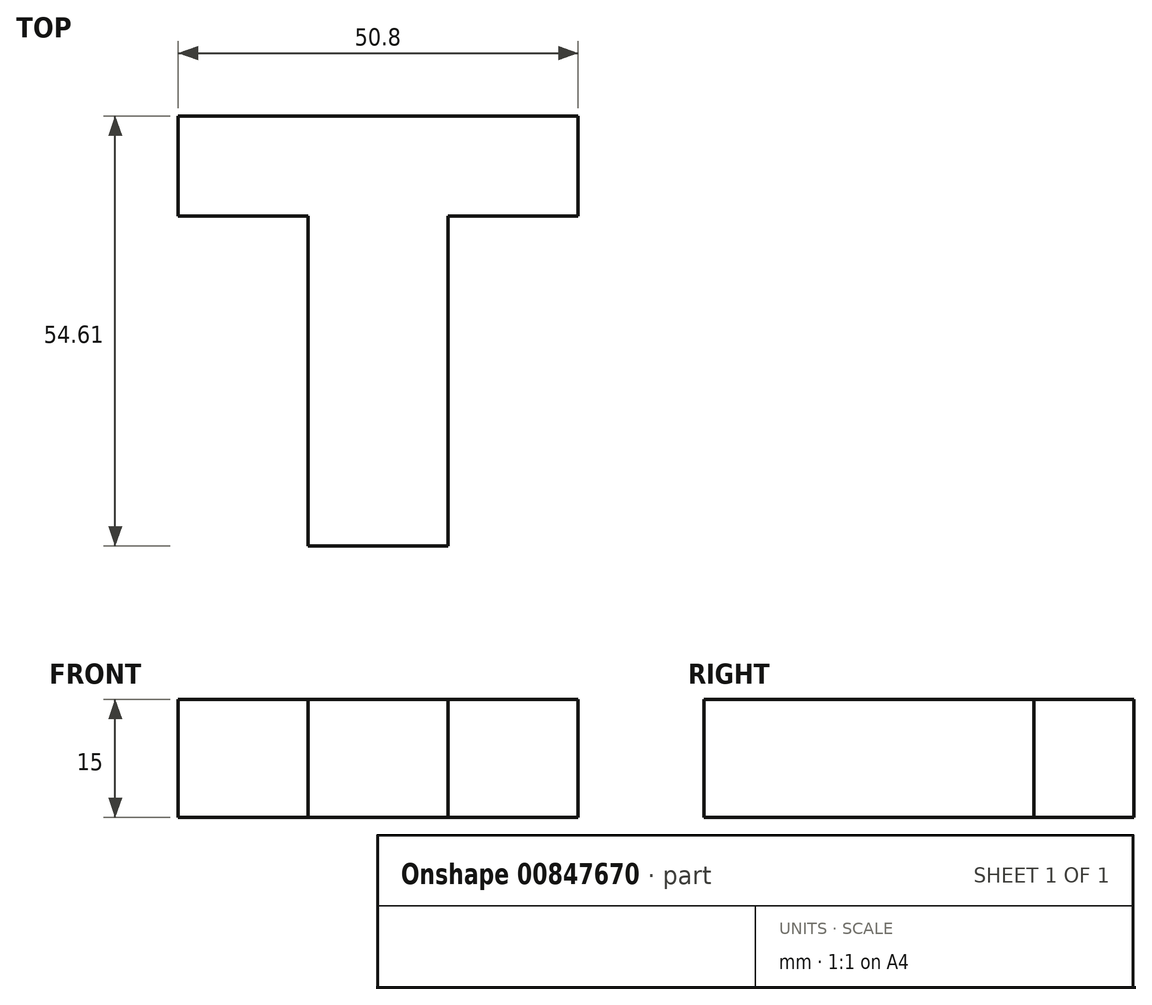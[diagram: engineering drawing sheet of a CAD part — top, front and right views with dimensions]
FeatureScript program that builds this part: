
annotation { "Feature Type Name" : "Feature", "Feature Type Description" : "" }
export const myFeature = defineFeature(function(context is Context, id is Id, definition is map)
    precondition{}
    {
        {
            var Q0;
            Q0=qCreatedBy(makeId("Top.planeOp"),FACE);
            var sketch = newSketch(context, id + "F0", { "sketchPlane" : qUnion([Q0])});
            skLineSegment(sketch, "E0", {"start": v(34.3, 0) * mm, "end": v(34.3, 12.7) * mm});
            skLineSegment(sketch, "E1", {"start": v(34.3, 12.7) * mm, "end": v(-16.51, 12.7) * mm});
            skLineSegment(sketch, "E2", {"start": v(-16.51, 12.7) * mm, "end": v(-16.51, 0) * mm});
            skPoint(sketch, "E3.end.orphan", {"position": v(17.78, 0) * mm});
            skLineSegment(sketch, "E4", {"start": v(-16.51, 0) * mm, "end": v(0, 0) * mm});
            skLineSegment(sketch, "E5", {"start": v(34.3, 0) * mm, "end": v(17.78, 0) * mm});
            skLineSegment(sketch, "E6", {"start": v(0, 0) * mm, "end": v(0, -41.91) * mm});
            skLineSegment(sketch, "E7", {"start": v(0, -41.91) * mm, "end": v(17.78, -41.91) * mm});
            skLineSegment(sketch, "E8", {"start": v(17.78, -41.91) * mm, "end": v(17.78, 0) * mm});
            skSolve(sketch);
        }
        {
            var Q0;
            Q0=makeQuery(id+"F0.imprint","IMPRINT",FACE,{"disambiguationData":[TD([[makeQuery(id+"F0.imprint","IMPRINT",EDGE,{"derivedFrom":sQuery(id+"F0.wireOp",EDGE,"E0")}),1.0]])]});
            extrude(context, id + "F1", {"entities" : qUnion([Q0]), "depth" : 15 * mm, "offsetDistance" : 25 * mm});
        }
    });
